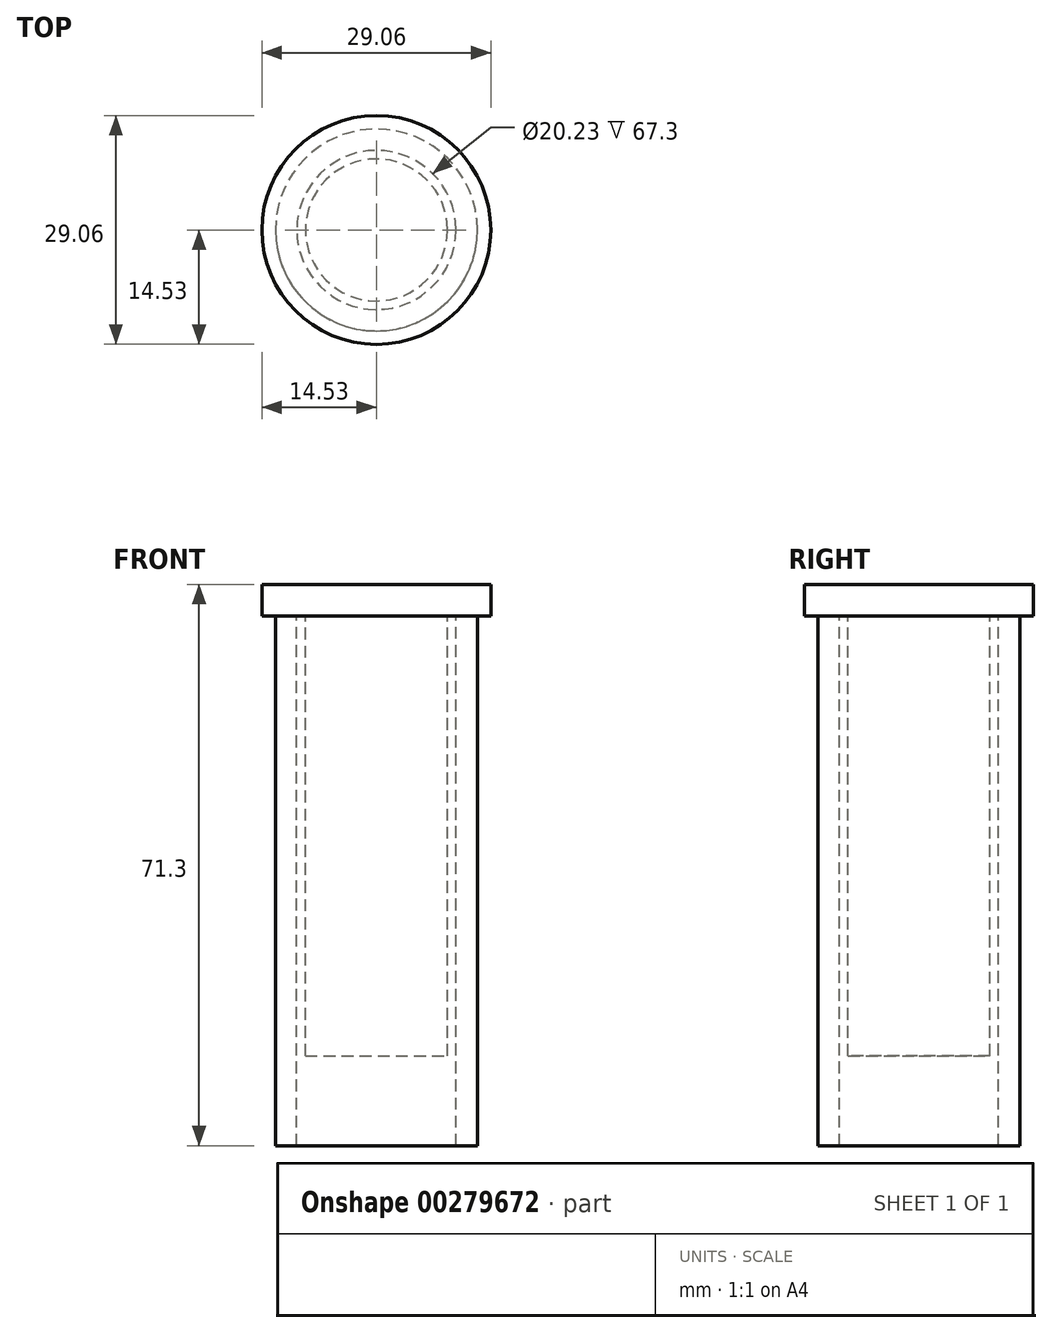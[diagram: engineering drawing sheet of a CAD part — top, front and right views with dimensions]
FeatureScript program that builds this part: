
annotation { "Feature Type Name" : "Feature", "Feature Type Description" : "" }
export const myFeature = defineFeature(function(context is Context, id is Id, definition is map)
    precondition{}
    {
        {
            var Q0;
            Q0=qCreatedBy(makeId("Top.planeOp"),FACE);
            var sketch = newSketch(context, id + "F0", { "sketchPlane" : qUnion([Q0])});
            skCircle(sketch, "E0", {"center": v(0, 0) * mm, "radius": 14.53 * mm});
            skSolve(sketch);
        }
        {
            var Q0;
            Q0=makeQuery(id+"F0.imprint","IMPRINT",FACE,{"disambiguationData":[TD([[makeQuery(id+"F0.imprint","IMPRINT",EDGE,{"derivedFrom":sQuery(id+"F0.wireOp",EDGE,"E0")}),1.0]])]});
            extrude(context, id + "F1", {"entities" : qUnion([Q0]), "oppositeDirection" : true, "depth" : 4 * mm});
        }
        {
            var Q0;
            Q0=makeQuery(id+"F1.opExtrude","CAP_FACE",FACE,{"disambiguationData":[OSD([sQuery(id+"F0.wireOp",EDGE,"E0")])],"isStart":false});
            var sketch = newSketch(context, id + "F2", { "sketchPlane" : qUnion([Q0])});
            skCircle(sketch, "E1", {"center": v(0, 0) * mm, "radius": 9.02 * mm});
            skSolve(sketch);
        }
        {
            var Q0;
            Q0=makeQuery(id+"F2.imprint","IMPRINT",FACE,{"disambiguationData":[TD([[makeQuery(id+"F2.imprint","IMPRINT",EDGE,{"derivedFrom":sQuery(id+"F2.wireOp",EDGE,"E1")}),1.0]])]});
            extrude(context, id + "F3", {"entities" : qUnion([Q0]), "operationType" : NewBodyOperationType.ADD, "depth" : 55.9 * mm});
        }
        {
            var Q0;
            Q0=makeQuery(id+"F1.opExtrude","CAP_FACE",FACE,{"disambiguationData":[OSD([sQuery(id+"F0.wireOp",EDGE,"E0")])],"isStart":false});
            var sketch = newSketch(context, id + "F4", { "sketchPlane" : qUnion([Q0])});
            skCircle(sketch, "E2", {"center": v(0, 0) * mm, "radius": 10.11 * mm});
            skCircle(sketch, "E3", {"center": v(0, 0) * mm, "radius": 12.83 * mm});
            skSolve(sketch);
        }
        {
            var Q0;
            Q0=makeQuery(id+"F4.imprint","IMPRINT",FACE,{"disambiguationData":[TD([[makeQuery(id+"F4.imprint","IMPRINT",EDGE,{"derivedFrom":sQuery(id+"F4.wireOp",EDGE,"E2")}),-1.0]])]});
            extrude(context, id + "F5", {"entities" : qUnion([Q0]), "operationType" : NewBodyOperationType.ADD, "depth" : 67.3 * mm});
        }
    });
